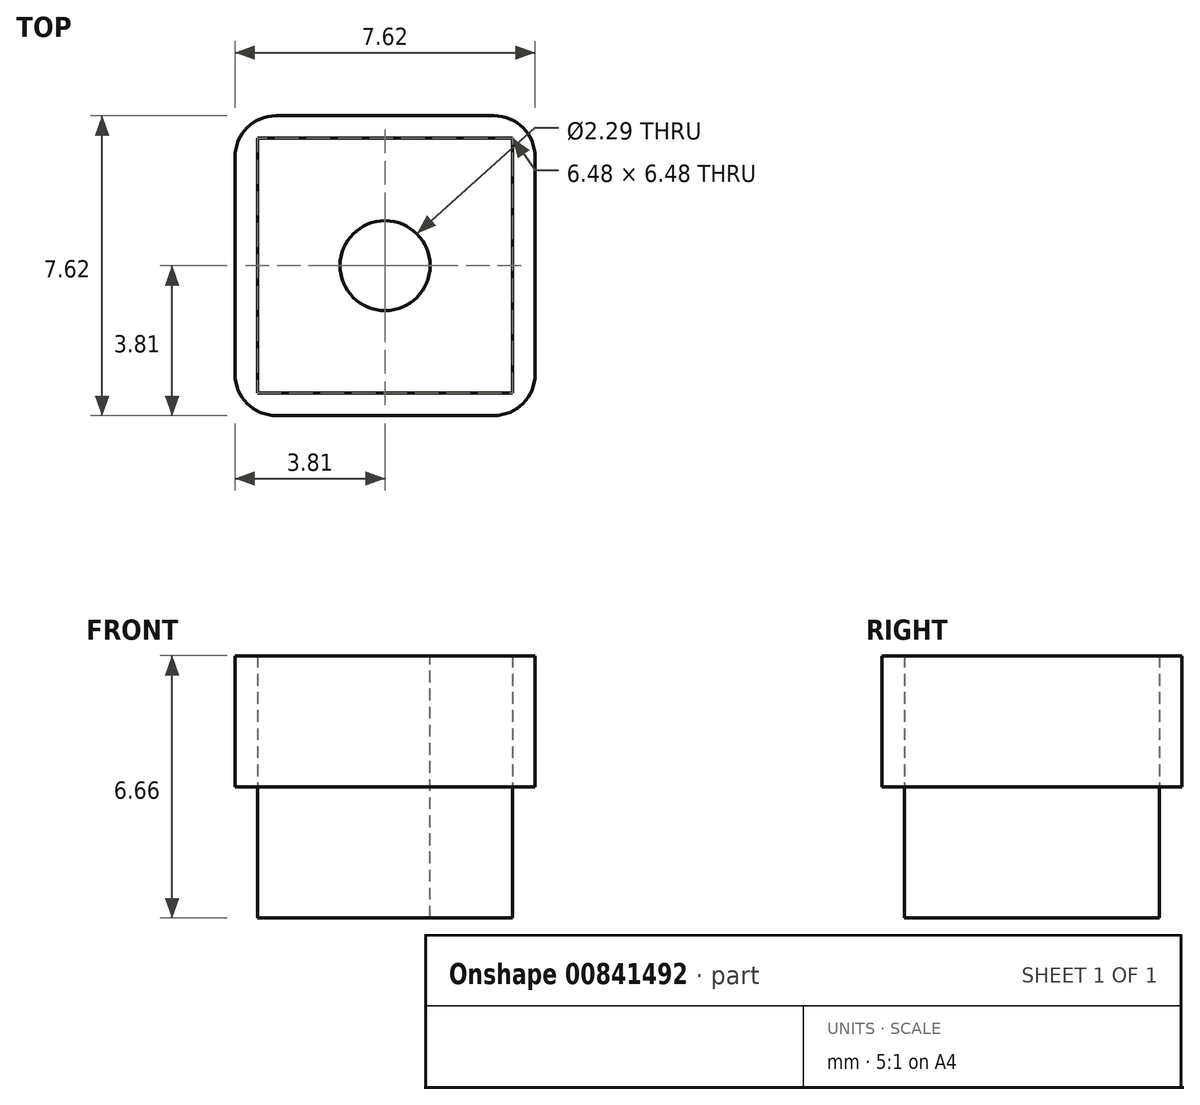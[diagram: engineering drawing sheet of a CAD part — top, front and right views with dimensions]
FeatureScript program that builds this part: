
annotation { "Feature Type Name" : "Feature", "Feature Type Description" : "" }
export const myFeature = defineFeature(function(context is Context, id is Id, definition is map)
    precondition{}
    {
        {
            var Q0;
            Q0=qCreatedBy(makeId("Top.planeOp"),FACE);
            var sketch = newSketch(context, id + "F0", { "sketchPlane" : qUnion([Q0])});
            skCircle(sketch, "E0", {"center": v(0, 0) * mm, "radius": 1.14 * mm});
            skLineSegment(sketch, "E1.bottom", {"start": v(3.24, -3.24) * mm, "end": v(-3.24, -3.24) * mm});
            skLineSegment(sketch, "E1.top", {"start": v(3.24, 3.24) * mm, "end": v(-3.24, 3.24) * mm});
            skLineSegment(sketch, "E1.left", {"start": v(3.24, -3.24) * mm, "end": v(3.24, 3.24) * mm});
            skLineSegment(sketch, "E1.right", {"start": v(-3.24, -3.24) * mm, "end": v(-3.24, 3.24) * mm});
            skLineSegment(sketch, "E2.bottom", {"start": v(3.81, -3.8) * mm, "end": v(-3.8, -3.8) * mm});
            skLineSegment(sketch, "E2.top", {"start": v(3.8, 3.81) * mm, "end": v(-3.81, 3.8) * mm});
            skLineSegment(sketch, "E2.left", {"start": v(3.81, -3.8) * mm, "end": v(3.8, 3.81) * mm});
            skLineSegment(sketch, "E2.right", {"start": v(-3.8, -3.81) * mm, "end": v(-3.81, 3.8) * mm});
            skSolve(sketch);
        }
        {
            var Q0;
            Q0=makeQuery(id+"F0.imprint","IMPRINT",FACE,{"disambiguationData":[TD([[makeQuery(id+"F0.imprint","IMPRINT",EDGE,{"derivedFrom":sQuery(id+"F0.wireOp",EDGE,"E0")}),-1.0]])]});
            extrude(context, id + "F1", {"entities" : qUnion([Q0]), "endBound" : BoundingType.SYMMETRIC, "oppositeDirection" : true, "depth" : 6.65 * mm, "offsetDistance" : 25.4 * mm});
        }
        {
            var Q0;
            Q0 = qSketchRegion(id + "F0", true);
            extrude(context, id + "F2", {"entities" : qUnion([Q0]), "depth" : 3.33 * mm, "offsetDistance" : 25.4 * mm});
        }
        {
            var Q0;
            Q0=makeQuery(id+"F2.opExtrude","SWEPT_EDGE",EDGE,{"disambiguationData":[OSD([sQuery(id+"F0.wireOp",EDGE,"E2.top"),sQuery(id+"F0.wireOp",EDGE,"E2.right")])]});
            var Q1;
            Q1=makeQuery(id+"F2.opExtrude","SWEPT_EDGE",EDGE,{"disambiguationData":[OSD([sQuery(id+"F0.wireOp",EDGE,"E2.bottom"),sQuery(id+"F0.wireOp",EDGE,"E2.right")])]});
            var Q2;
            Q2=makeQuery(id+"F2.opExtrude","SWEPT_EDGE",EDGE,{"disambiguationData":[OSD([sQuery(id+"F0.wireOp",EDGE,"E2.bottom"),sQuery(id+"F0.wireOp",EDGE,"E2.left")])]});
            var Q3;
            Q3=makeQuery(id+"F2.opExtrude","SWEPT_EDGE",EDGE,{"disambiguationData":[OSD([sQuery(id+"F0.wireOp",EDGE,"E2.top"),sQuery(id+"F0.wireOp",EDGE,"E2.left")])]});
            fillet(context, id + "F3", {"entities" : qUnion([Q0, Q1, Q2, Q3]), "radius" : 1.04 * mm, "tangentPropagation" : true, "allowEdgeOverflow" : false});
        }
    });
